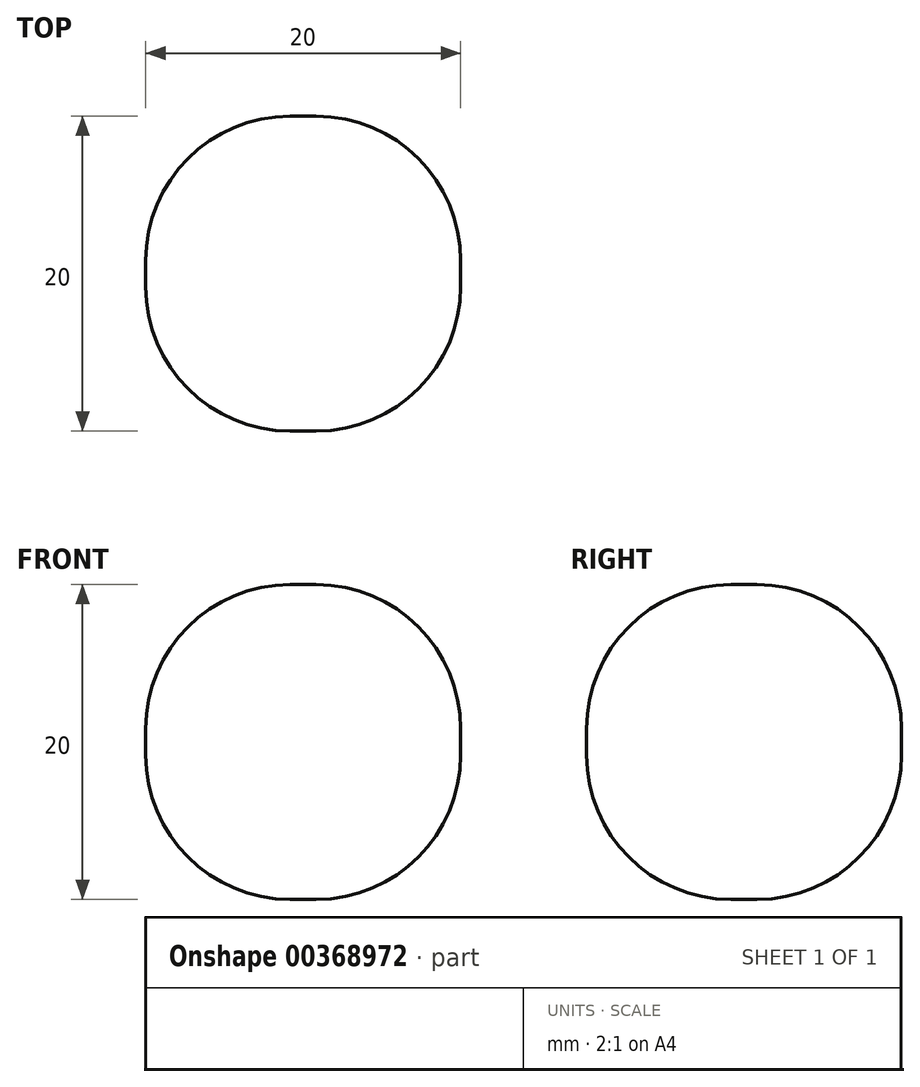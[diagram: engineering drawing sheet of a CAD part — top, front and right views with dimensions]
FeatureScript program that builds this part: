
annotation { "Feature Type Name" : "Feature", "Feature Type Description" : "" }
export const myFeature = defineFeature(function(context is Context, id is Id, definition is map)
    precondition{}
    {
        {
            var Q0;
            Q0=qCreatedBy(makeId("Top.planeOp"),FACE);
            var sketch = newSketch(context, id + "F0", { "sketchPlane" : qUnion([Q0])});
            skLineSegment(sketch, "E0.bottom", {"start": v(-111.55, 11.9) * mm, "end": v(-91.55, 11.9) * mm});
            skLineSegment(sketch, "E0.top", {"start": v(-111.55, -8.1) * mm, "end": v(-91.55, -8.1) * mm});
            skLineSegment(sketch, "E0.left", {"start": v(-111.55, 11.9) * mm, "end": v(-111.55, -8.1) * mm});
            skLineSegment(sketch, "E0.right", {"start": v(-91.55, 11.9) * mm, "end": v(-91.55, -8.1) * mm});
            skSolve(sketch);
        }
        {
            var Q0;
            Q0 = qSketchRegion(id + "F0", true);
            extrude(context, id + "F1", {"entities" : qUnion([Q0]), "depth" : 20 * mm});
        }
        {
            var Q0;
            Q0=makeQuery(id+"F1.opExtrude","CAP_EDGE",EDGE,{"disambiguationData":[OSD([sQuery(id+"F0.wireOp",EDGE,"E0.top")])],"isStart":false});
            var Q1;
            Q1=makeQuery(id+"F1.opExtrude","CAP_EDGE",EDGE,{"disambiguationData":[OSD([sQuery(id+"F0.wireOp",EDGE,"E0.bottom")])],"isStart":false});
            var Q2;
            Q2=makeQuery(id+"F1.opExtrude","CAP_EDGE",EDGE,{"disambiguationData":[OSD([sQuery(id+"F0.wireOp",EDGE,"E0.right")])],"isStart":false});
            var Q3;
            Q3=makeQuery(id+"F1.opExtrude","CAP_EDGE",EDGE,{"disambiguationData":[OSD([sQuery(id+"F0.wireOp",EDGE,"E0.left")])],"isStart":false});
            var Q4;
            Q4=makeQuery(id+"F1.opExtrude","CAP_EDGE",EDGE,{"disambiguationData":[OSD([sQuery(id+"F0.wireOp",EDGE,"E0.top")])],"isStart":true});
            var Q5;
            Q5=makeQuery(id+"F1.opExtrude","SWEPT_EDGE",EDGE,{"disambiguationData":[OSD([sQuery(id+"F0.wireOp",EDGE,"E0.top"),sQuery(id+"F0.wireOp",EDGE,"E0.right")])]});
            var Q6;
            Q6=makeQuery(id+"F1.opExtrude","SWEPT_EDGE",EDGE,{"disambiguationData":[OSD([sQuery(id+"F0.wireOp",EDGE,"E0.top"),sQuery(id+"F0.wireOp",EDGE,"E0.left")])]});
            var Q7;
            Q7=makeQuery(id+"F1.opExtrude","SWEPT_EDGE",EDGE,{"disambiguationData":[OSD([sQuery(id+"F0.wireOp",EDGE,"E0.bottom"),sQuery(id+"F0.wireOp",EDGE,"E0.right")])]});
            var Q8;
            Q8=makeQuery(id+"F1.opExtrude","SWEPT_EDGE",EDGE,{"disambiguationData":[OSD([sQuery(id+"F0.wireOp",EDGE,"E0.bottom"),sQuery(id+"F0.wireOp",EDGE,"E0.left")])]});
            var Q9;
            Q9=makeQuery(id+"F1.opExtrude","CAP_EDGE",EDGE,{"disambiguationData":[OSD([sQuery(id+"F0.wireOp",EDGE,"E0.bottom")])],"isStart":true});
            var Q10;
            Q10=makeQuery(id+"F1.opExtrude","CAP_EDGE",EDGE,{"disambiguationData":[OSD([sQuery(id+"F0.wireOp",EDGE,"E0.right")])],"isStart":true});
            var Q11;
            Q11=makeQuery(id+"F1.opExtrude","CAP_EDGE",EDGE,{"disambiguationData":[OSD([sQuery(id+"F0.wireOp",EDGE,"E0.left")])],"isStart":true});
            fillet(context, id + "F2", {"entities" : qUnion([Q0, Q1, Q2, Q3, Q4, Q5, Q6, Q7, Q8, Q9, Q10, Q11]), "radius" : 9.17 * mm, "tangentPropagation" : true, "allowEdgeOverflow" : false});
        }
    });
